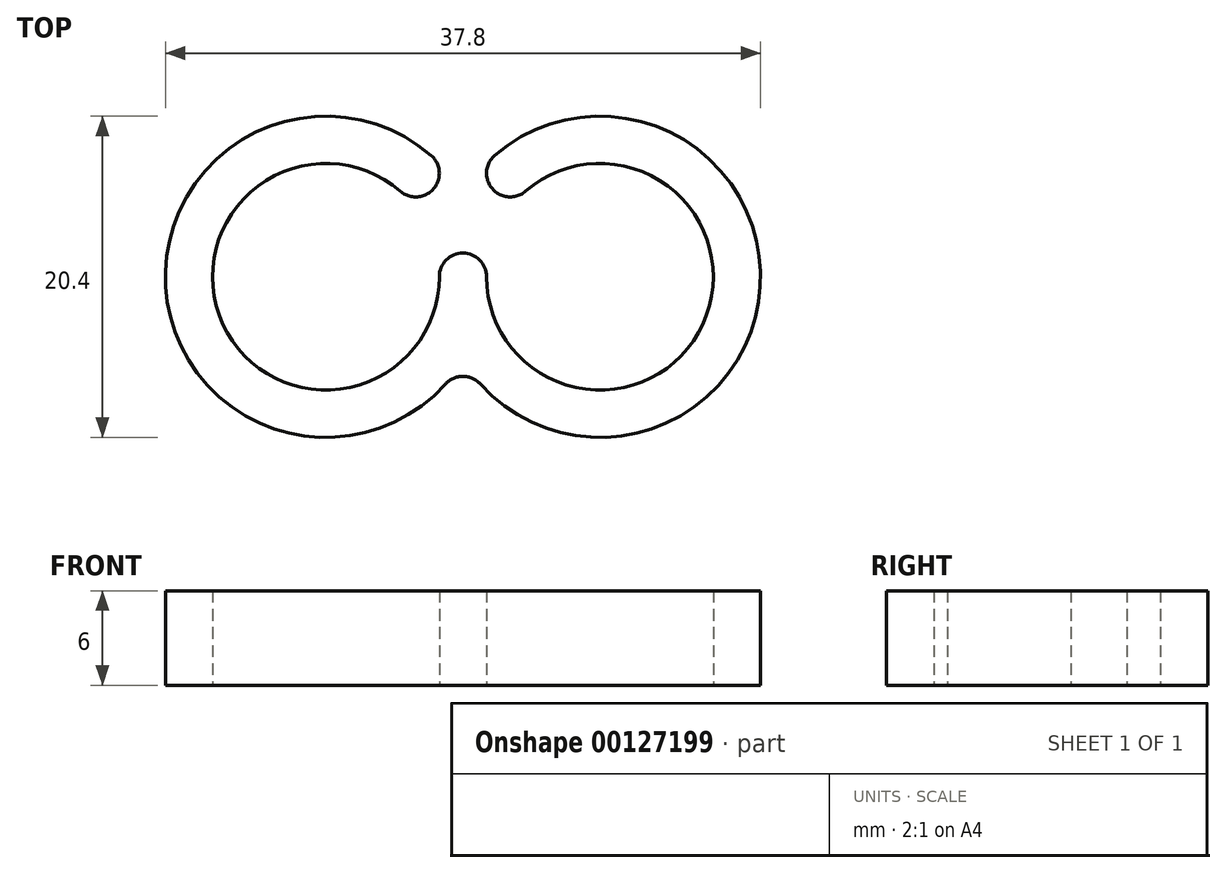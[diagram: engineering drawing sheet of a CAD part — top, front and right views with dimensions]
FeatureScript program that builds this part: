
annotation { "Feature Type Name" : "Feature", "Feature Type Description" : "" }
export const myFeature = defineFeature(function(context is Context, id is Id, definition is map)
    precondition{}
    {
        {
            var Q0;
            Q0=qCreatedBy(makeId("Top.planeOp"),FACE);
            var sketch = newSketch(context, id + "F0", { "sketchPlane" : qUnion([Q0])});
            skCircle(sketch, "E0", {"center": v(8.7, 0) * mm, "radius": 7.2 * mm});
            skCircle(sketch, "E1.MirrorC", {"center": v(-8.7, 0) * mm, "radius": 7.2 * mm});
            skArc(sketch, "E2", {"start": v(1.12, -6.82) * mm, "mid": v(18.88, -0.63) * mm, "end": v(2.02, 7.7) * mm});
            skArc(sketch, "E3.MirrorC", {"start": v(-1.12, -6.82) * mm, "mid": v(-18.88, -0.63) * mm, "end": v(-2.02, 7.7) * mm});
            skCircle(sketch, "E4", {"center": v(8.7, 0) * mm, "radius": 3 * mm});
            skCircle(sketch, "E5.MirrorC", {"center": v(-8.7, 0) * mm, "radius": 3 * mm});
            skArc(sketch, "E6.filletArc", {"start": v(1.12, -6.82) * mm, "mid": v(0, -6.32) * mm, "end": v(-1.12, -6.82) * mm});
            skArc(sketch, "E7", {"start": v(2.02, 7.7) * mm, "mid": v(1.87, 5.59) * mm, "end": v(3.98, 5.44) * mm});
            skLineSegment(sketch, "E8", {"start": v(8.7, 0) * mm, "end": v(3, 6.57) * mm, "construction": true});
            skArc(sketch, "E9", {"start": v(1.5, 0) * mm, "mid": v(0, 1.5) * mm, "end": v(-1.5, 0) * mm});
            skArc(sketch, "E10", {"start": v(-3.98, 5.44) * mm, "mid": v(-1.87, 5.59) * mm, "end": v(-2.02, 7.7) * mm});
            skLineSegment(sketch, "E11", {"start": v(-8.7, 0) * mm, "end": v(-3, 6.57) * mm, "construction": true});
            skSolve(sketch);
        }
        {
            var Q0;
            Q0=makeQuery(id+"F0.imprint","IMPRINT",FACE,{"disambiguationData":[TD([[makeQuery(id+"F0.imprint","IMPRINT",EDGE,{"derivedFrom":sQuery(id+"F0.wireOp",EDGE,"E2")}),1.0]])]});
            extrude(context, id + "F1", {"entities" : qUnion([Q0]), "depth" : 6 * mm});
        }
    });
